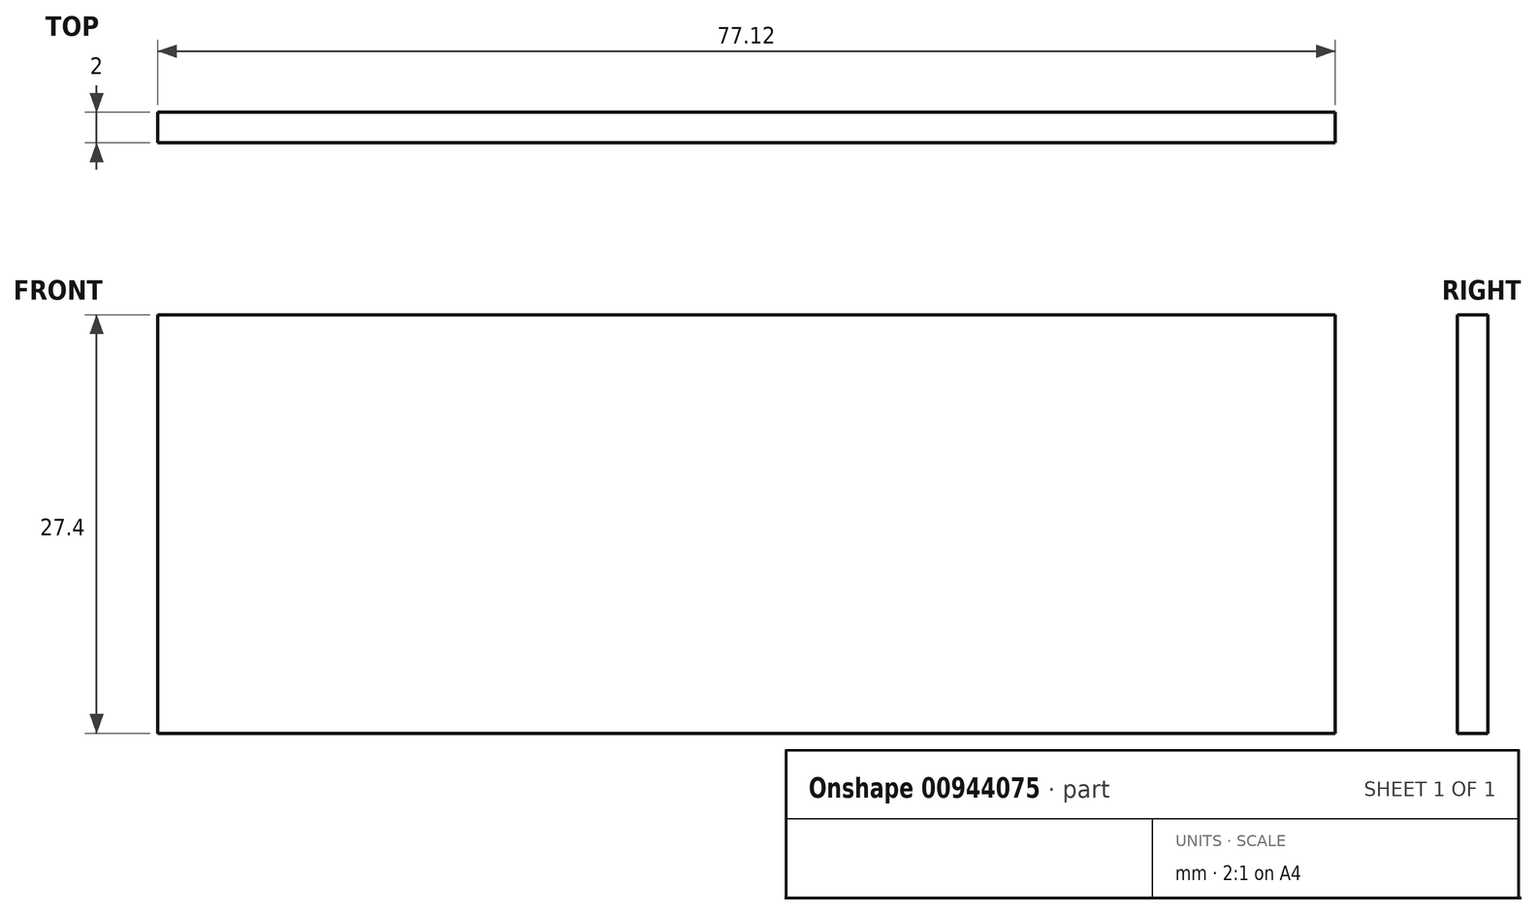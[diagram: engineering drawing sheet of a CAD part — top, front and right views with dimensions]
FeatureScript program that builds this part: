
annotation { "Feature Type Name" : "Feature", "Feature Type Description" : "" }
export const myFeature = defineFeature(function(context is Context, id is Id, definition is map)
    precondition{}
    {
        {
            var Q0;
            Q0=qCreatedBy(makeId("Front.planeOp"),FACE);
            var sketch = newSketch(context, id + "F0", { "sketchPlane" : qUnion([Q0])});
            skLineSegment(sketch, "E0.bottom", {"start": v(0, 27.4) * mm, "end": v(77.12, 27.4) * mm});
            skLineSegment(sketch, "E0.top", {"start": v(0, 0) * mm, "end": v(77.12, 0) * mm});
            skLineSegment(sketch, "E0.left", {"start": v(0, 27.4) * mm, "end": v(0, 0) * mm});
            skLineSegment(sketch, "E0.right", {"start": v(77.12, 27.4) * mm, "end": v(77.12, 0) * mm});
            skSolve(sketch);
        }
        {
            var Q0;
            Q0=qSketchRegion(id+"F0",true);
            extrude(context, id + "F1", {"entities" : qUnion([Q0]), "depth" : 2 * mm, "offsetDistance" : 25 * mm});
        }
    });
